# Revit family: TESK_Насос вертикальный_SVM(T)-5
name_source: partatom
category: Оборудование
units: mm (PartAtom-declared; Revit-internal decimal feet)

## family parameters
Всегда вертикально = Да
Классификация = Насос
На основе рабочей плоскости = Нет
Общий = Нет
При загрузке вырезать с полостями = Нет
Размер круглого соединителя = Использовать диаметр
Тип детали = Вставляется
Точка расчета площади = Нет

## types (36) — shared parameters
ADSK_Версия Revit = 2019
ADSK_Версия семейства = 1.0
ADSK_Диаметр условный = 32 мм
ADSK_Единица измерения = шт.
ADSK_Завод-изготовитель = TESK
ADSK_Классификация нагрузок = Прочее
ADSK_Количество = 1
ADSK_Количество фаз = 3
ADSK_Количество фаз числовое = 3
ADSK_Коэффициент мощности = 1
ADSK_Наименование краткое = Вертикальный многоступенчатый центробежный насос
ADSK_Напряжение = 400 В
URL = www.teskpump.ru
Длина_ВспомЛиния = 30 мм
Материал_1 = TESK_Черный_Условный
Материал_2 = TESK_Нержавеющая сталь
Материал_КорпусДвигателя = TESK_Черный_Ребра_Условный
Таблица_Поиска = TESK_SVM(T)-5
УГО_Длина = 250 мм
Фланец_Толщина = 20 мм

## per-type parameters (varying)
| type | ADSK_Код изделия | ADSK_Масса | ADSK_Масса_Текст | ADSK_Наименование | ADSK_Номинальная мощность | ADSK_Полная мощность | Высота_Корпуса | Высота_Перехода | Двигатель_Высота | Двигатель_ОтступКоробки | Двигатель_Ширина | Материал_КорпусУлитка | Напор максимальный |
| SVM 5-2 0.37kW 3x380V 50Hz IE3 | 775-200003380NSSF | 21 | 21 | Вертикальный многоступенчатый центробежный насос SVM, DN32, PN25, Hmax=12.5м (3x380V 50Hz IE3) | 0 кВт | 0 кВ·А | 276 мм | 90 мм | 239 мм | 117 мм | 148 мм | TESK_Нержавеющая сталь | 12.5 |
| SVM 5-3 0.55kW 3x380V 50Hz IE3 | 775-300003380NSSF | 22 | 22 | Вертикальный многоступенчатый центробежный насос SVM, DN32, PN25, Hmax=19.5м (3x380V 50Hz IE3) | 1 кВт | 1 кВ·А | 303 мм | 90 мм | 239 мм | 117 мм | 148 мм | TESK_Нержавеющая сталь | 19.5 |
| SVM 5-4 0.55kW 3x380V 50Hz IE3 | 775-400003380NSSF | 23 | 23 | Вертикальный многоступенчатый центробежный насос SVM, DN32, PN25, Hmax=26м (3x380V 50Hz IE3) | 1 кВт | 1 кВ·А | 330 мм | 90 мм | 239 мм | 117 мм | 148 мм | TESK_Нержавеющая сталь | 26 |
| SVM 5-5 0.75kW 3x380V 50Hz IE3 | 775-500003380NSSF | 25 | 25 | Вертикальный многоступенчатый центробежный насос SVM, DN32, PN25, Hmax=32.5м (3x380V 50Hz IE3) | 1 кВт | 1 кВ·А | 367 мм | 110 мм | 280 мм | 142 мм | 170 мм | TESK_Нержавеющая сталь | 32.5 |
| SVM 5-6 1.1kW 3x380V 50Hz IE3 | 775-600003380NSSF | 26 | 26 | Вертикальный многоступенчатый центробежный насос SVM, DN32, PN25, Hmax=38.5м (3x380V 50Hz IE3) | 1 кВт | 1 кВ·А | 394 мм | 110 мм | 280 мм | 142 мм | 170 мм | TESK_Нержавеющая сталь | 38.5 |
| SVM 5-8 1.1kW 3x380V 50Hz IE3 | 775-800003380NSSF | 27 | 27 | Вертикальный многоступенчатый центробежный насос SVM, DN32, PN25, Hmax=50.5м (3x380V 50Hz IE3) | 1 кВт | 1 кВ·А | 448 мм | 110 мм | 280 мм | 142 мм | 170 мм | TESK_Нержавеющая сталь | 50.5 |
| SVM 5-10 1.5kW 3x380V 50Hz IE3 | 775-100003380NSSF | 33 | 33 | Вертикальный многоступенчатый центробежный насос SVM, DN32, PN25, Hmax=63.5м (3x380V 50Hz IE3) | 2 кВт | 2 кВ·А | 512 мм | 130 мм | 333 мм | 155 мм | 190 мм | TESK_Нержавеющая сталь | 63.5 |
| SVM 5-12 2.2kW 3x380V 50Hz IE3 | 775-120003380NSSF | 37 | 37 | Вертикальный многоступенчатый центробежный насос SVM, DN32, PN25, Hmax=76м (3x380V 50Hz IE3) | 2 кВт | 2 кВ·А | 566 мм | 130 мм | 333 мм | 155 мм | 190 мм | TESK_Нержавеющая сталь | 76 |
| SVM 5-14 2.2kW 3x380V 50Hz IE3 | 775-140003380NSSF | 38 | 38 | Вертикальный многоступенчатый центробежный насос SVM, DN32, PN25, Hmax=89м (3x380V 50Hz IE3) | 2 кВт | 2 кВ·А | 620 мм | 130 мм | 333 мм | 155 мм | 190 мм | TESK_Нержавеющая сталь | 89 |
| SVM 5-16 2.2kW 3x380V 50Hz IE3 | 775-160003380NSSF | 39 | 39 | Вертикальный многоступенчатый центробежный насос SVM, DN32, PN25, Hmax=101м (3x380V 50Hz IE3) | 2 кВт | 2 кВ·А | 674 мм | 130 мм | 333 мм | 155 мм | 190 мм | TESK_Нержавеющая сталь | 101 |
| SVM 5-18 3kW 3x380V 50Hz IE3 | 775-180003380NSSF | 48 | 48 | Вертикальный многоступенчатый центробежный насос SVM, DN32, PN25, Hmax=115м (3x380V 50Hz IE3) | 3 кВт | 3 кВ·А | 738 мм | 150 мм | 348 мм | 165 мм | 197 мм | TESK_Нержавеющая сталь | 115 |
| SVM 5-20 3kW 3x380V 50Hz IE3 | 775-2000003380NSSF | 49 | 49 | Вертикальный многоступенчатый центробежный насос SVM, DN32, PN25, Hmax=129м (3x380V 50Hz IE3) | 3 кВт | 3 кВ·А | 792 мм | 150 мм | 348 мм | 165 мм | 197 мм | TESK_Нержавеющая сталь | 129 |
| SVM 5-22 4kW 3x380V 50Hz IE3 | 775-2200003380NSSF | 57 | 57 | Вертикальный многоступенчатый центробежный насос SVM, DN32, PN25, Hmax=142м (3x380V 50Hz IE3) | 4 кВт | 4 кВ·А | 846 мм | 170 мм | 382 мм | 185 мм | 230 мм | TESK_Нержавеющая сталь | 142 |
| SVM 5-24 4kW 3x380V 50Hz IE3 | 775-2400003380NSSF | 58 | 58 | Вертикальный многоступенчатый центробежный насос SVM, DN32, PN25, Hmax=156м (3x380V 50Hz IE3) | 4 кВт | 4 кВ·А | 900 мм | 170 мм | 382 мм | 185 мм | 230 мм | TESK_Нержавеющая сталь | 156 |
| SVM 5-26 4kW 3x380V 50Hz IE3 | 775-2600003380NSSF | 59 | 59 | Вертикальный многоступенчатый центробежный насос SVM, DN32, PN25, Hmax=169м (3x380V 50Hz IE3) | 4 кВт | 4 кВ·А | 954 мм | 170 мм | 382 мм | 185 мм | 230 мм | TESK_Нержавеющая сталь | 169 |
| SVM 5-29 4kW 3x380V 50Hz IE3 | 775-2900003380NSSF | 60 | 60 | Вертикальный многоступенчатый центробежный насос SVM, DN32, PN25, Hmax=189м (3x380V 50Hz IE3) | 4 кВт | 4 кВ·А | 1035 мм | 170 мм | 382 мм | 185 мм | 230 мм | TESK_Нержавеющая сталь | 189 |
| SVM 5-32 5.5kW 3x380V 50Hz IE3 | 775-3200003380NSSF | 75 | 75 | Вертикальный многоступенчатый центробежный насос SVM, DN32, PN25, Hmax=209м (3x380V 50Hz IE3) | 6 кВт | 6 кВ·А | 1136 мм | 190 мм | 435 мм | 210 мм | 260 мм | TESK_Нержавеющая сталь | 209 |
| SVM 5-36 5.5kW 3x380V 50Hz IE3 | 775-3600003380NSSF | 76 | 76 | Вертикальный многоступенчатый центробежный насос SVM, DN32, PN25, Hmax=232м (3x380V 50Hz IE3) | 6 кВт | 6 кВ·А | 1244 мм | 190 мм | 435 мм | 210 мм | 260 мм | TESK_Нержавеющая сталь | 232 |
| SVMT 5-2 0.37kW 3x380V 50Hz IE3 | 775-200003380N | 21 | 21 | Вертикальный многоступенчатый центробежный насос SVMT, DN32, PN25, Hmax=12.5м (3x380V 50Hz IE3) | 0 кВт | 0 кВ·А | 276 мм | 90 мм | 239 мм | 117 мм | 148 мм | TESK_Черный_Условный | 12.5 |
| SVMT 5-3 0.55kW 3x380V 50Hz IE3 | 775-300003380N | 22 | 22 | Вертикальный многоступенчатый центробежный насос SVMT, DN32, PN25, Hmax=19.5м (3x380V 50Hz IE3) | 1 кВт | 1 кВ·А | 303 мм | 90 мм | 239 мм | 117 мм | 148 мм | TESK_Черный_Условный | 19.5 |
| SVMT 5-4 0.55kW 3x380V 50Hz IE3 | 775-400003380N | 23 | 23 | Вертикальный многоступенчатый центробежный насос SVMT, DN32, PN25, Hmax=26м (3x380V 50Hz IE3) | 1 кВт | 1 кВ·А | 330 мм | 90 мм | 239 мм | 117 мм | 148 мм | TESK_Черный_Условный | 26 |
| SVMT 5-5 0.75kW 3x380V 50Hz IE3 | 775-500003380N | 25 | 25 | Вертикальный многоступенчатый центробежный насос SVMT, DN32, PN25, Hmax=32.5м (3x380V 50Hz IE3) | 1 кВт | 1 кВ·А | 367 мм | 110 мм | 280 мм | 142 мм | 170 мм | TESK_Черный_Условный | 32.5 |
| SVMT 5-6 1.1kW 3x380V 50Hz IE3 | 775-600003380N | 26 | 26 | Вертикальный многоступенчатый центробежный насос SVMT, DN32, PN25, Hmax=38.5м (3x380V 50Hz IE3) | 1 кВт | 1 кВ·А | 394 мм | 110 мм | 280 мм | 142 мм | 170 мм | TESK_Черный_Условный | 38.5 |
| SVMT 5-8 1.1kW 3x380V 50Hz IE3 | 775-800003380N | 27 | 27 | Вертикальный многоступенчатый центробежный насос SVMT, DN32, PN25, Hmax=50.5м (3x380V 50Hz IE3) | 1 кВт | 1 кВ·А | 448 мм | 110 мм | 280 мм | 142 мм | 170 мм | TESK_Черный_Условный | 50.5 |
| SVMT 5-10 1.5kW 3x380V 50Hz IE3 | 775-100003380N | 33 | 33 | Вертикальный многоступенчатый центробежный насос SVMT, DN32, PN25, Hmax=63.5м (3x380V 50Hz IE3) | 2 кВт | 2 кВ·А | 512 мм | 130 мм | 333 мм | 155 мм | 190 мм | TESK_Черный_Условный | 63.5 |
| SVMT 5-12 2.2kW 3x380V 50Hz IE3 | 775-120003380N | 37 | 37 | Вертикальный многоступенчатый центробежный насос SVMT, DN32, PN25, Hmax=76м (3x380V 50Hz IE3) | 2 кВт | 2 кВ·А | 566 мм | 130 мм | 333 мм | 155 мм | 190 мм | TESK_Черный_Условный | 76 |
| SVMT 5-14 2.2kW 3x380V 50Hz IE3 | 775-140003380N | 38 | 38 | Вертикальный многоступенчатый центробежный насос SVMT, DN32, PN25, Hmax=89м (3x380V 50Hz IE3) | 2 кВт | 2 кВ·А | 620 мм | 130 мм | 333 мм | 155 мм | 190 мм | TESK_Черный_Условный | 89 |
| SVMT 5-16 2.2kW 3x380V 50Hz IE3 | 775-160003380N | 39 | 39 | Вертикальный многоступенчатый центробежный насос SVMT, DN32, PN25, Hmax=101м (3x380V 50Hz IE3) | 2 кВт | 2 кВ·А | 674 мм | 130 мм | 333 мм | 155 мм | 190 мм | TESK_Черный_Условный | 101 |
| SVMT 5-18 3kW 3x380V 50Hz IE3 | 775-180003380N | 48 | 48 | Вертикальный многоступенчатый центробежный насос SVMT, DN32, PN25, Hmax=115м (3x380V 50Hz IE3) | 3 кВт | 3 кВ·А | 738 мм | 150 мм | 348 мм | 165 мм | 197 мм | TESK_Черный_Условный | 115 |
| SVMT 5-20 3kW 3x380V 50Hz IE3 | 775-2000003380N | 49 | 49 | Вертикальный многоступенчатый центробежный насос SVMT, DN32, PN25, Hmax=129м (3x380V 50Hz IE3) | 3 кВт | 3 кВ·А | 792 мм | 150 мм | 348 мм | 165 мм | 197 мм | TESK_Черный_Условный | 129 |
| SVMT 5-22 4kW 3x380V 50Hz IE3 | 775-2200003380N | 57 | 57 | Вертикальный многоступенчатый центробежный насос SVMT, DN32, PN25, Hmax=142м (3x380V 50Hz IE3) | 4 кВт | 4 кВ·А | 846 мм | 170 мм | 382 мм | 185 мм | 230 мм | TESK_Черный_Условный | 142 |
| SVMT 5-24 4kW 3x380V 50Hz IE3 | 775-2400003380N | 58 | 58 | Вертикальный многоступенчатый центробежный насос SVMT, DN32, PN25, Hmax=156м (3x380V 50Hz IE3) | 4 кВт | 4 кВ·А | 900 мм | 170 мм | 382 мм | 185 мм | 230 мм | TESK_Черный_Условный | 156 |
| SVMT 5-26 4kW 3x380V 50Hz IE3 | 775-2600003380N | 59 | 59 | Вертикальный многоступенчатый центробежный насос SVMT, DN32, PN25, Hmax=169м (3x380V 50Hz IE3) | 4 кВт | 4 кВ·А | 954 мм | 170 мм | 382 мм | 185 мм | 230 мм | TESK_Черный_Условный | 169 |
| SVMT 5-29 4kW 3x380V 50Hz IE3 | 775-2900003380N | 60 | 60 | Вертикальный многоступенчатый центробежный насос SVMT, DN32, PN25, Hmax=189м (3x380V 50Hz IE3) | 4 кВт | 4 кВ·А | 1035 мм | 170 мм | 382 мм | 185 мм | 230 мм | TESK_Черный_Условный | 189 |
| SVMT 5-32 5.5kW 3x380V 50Hz IE3 | 775-3200003380N | 75 | 75 | Вертикальный многоступенчатый центробежный насос SVMT, DN32, PN25, Hmax=209м (3x380V 50Hz IE3) | 6 кВт | 6 кВ·А | 1136 мм | 190 мм | 435 мм | 210 мм | 260 мм | TESK_Черный_Условный | 209 |
| SVMT 5-36 5.5kW 3x380V 50Hz IE3 | 775-3600003380N | 76 | 76 | Вертикальный многоступенчатый центробежный насос SVMT, DN32, PN25, Hmax=232м (3x380V 50Hz IE3) | 6 кВт | 6 кВ·А | 1244 мм | 190 мм | 435 мм | 210 мм | 260 мм | TESK_Черный_Условный | 232 |

note: column(s) folded — value = type name in every type: ADSK_Марка
